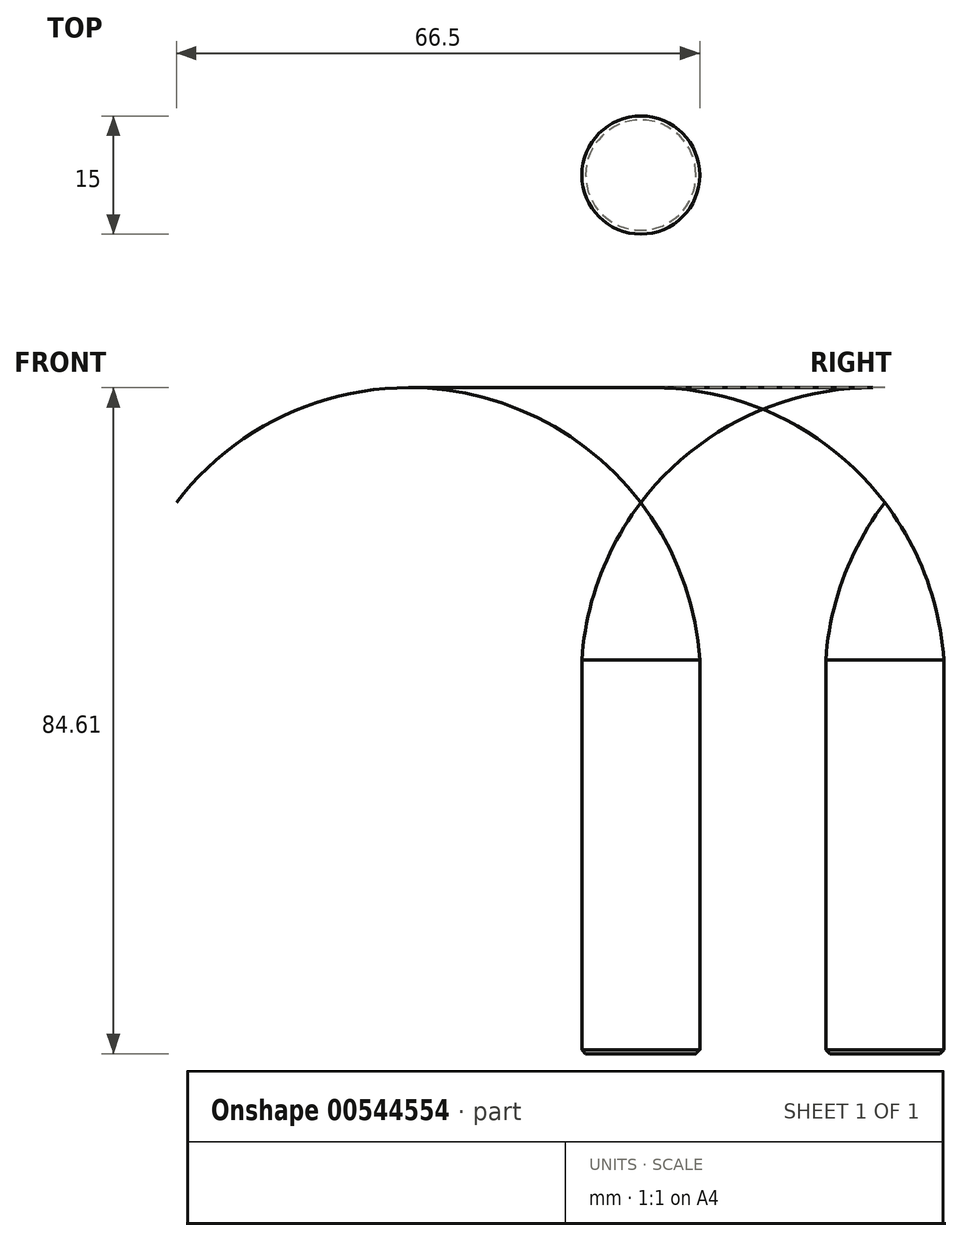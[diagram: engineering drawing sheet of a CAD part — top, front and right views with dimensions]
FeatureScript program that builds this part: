
annotation { "Feature Type Name" : "Feature", "Feature Type Description" : "" }
export const myFeature = defineFeature(function(context is Context, id is Id, definition is map)
    precondition{}
    {
        {
            var Q0;
            Q0=qCreatedBy(makeId("Front.planeOp"),FACE);
            var sketch = newSketch(context, id + "F0", { "sketchPlane" : qUnion([Q0])});
            skLineSegment(sketch, "E0", {"start": v(0, 0) * mm, "end": v(0, 20) * mm});
            skLineSegment(sketch, "E1", {"start": v(0, 0) * mm, "end": v(7.5, 0) * mm});
            skArc(sketch, "E2", {"start": v(7.5, 0) * mm, "mid": v(5.22, 10.55) * mm, "end": v(0, 20) * mm});
            skSolve(sketch);
        }
        {
            var Q0;
            Q0=makeQuery(id+"F0.imprint","IMPRINT",FACE,{"disambiguationData":[TD([[makeQuery(id+"F0.imprint","IMPRINT",EDGE,{"derivedFrom":sQuery(id+"F0.wireOp",EDGE,"E0")}),-1.0]])]});
            var Q1;
            Q1=sQuery(id+"F0.wireOp",EDGE,"E0");
            revolve(context, id + "F1", {"entities" : qUnion([Q0]), "axis" : qUnion([Q1]), "revolveType" : RevolveType.FULL});
        }
        {
            var Q0;
            Q0=qCreatedBy(makeId("Top.planeOp"),FACE);
            var sketch = newSketch(context, id + "F2", { "sketchPlane" : qUnion([Q0])});
            skCircle(sketch, "E3", {"center": v(0, 0) * mm, "radius": 7.5 * mm});
            skSolve(sketch);
        }
        {
            var Q0;
            Q0=makeQuery(id+"F2.imprint","IMPRINT",FACE,{"disambiguationData":[TD([[makeQuery(id+"F2.imprint","IMPRINT",EDGE,{"derivedFrom":sQuery(id+"F2.wireOp",EDGE,"E3")}),1.0]])]});
            extrude(context, id + "F3", {"entities" : qUnion([Q0]), "operationType" : NewBodyOperationType.ADD, "oppositeDirection" : true, "depth" : 50 * mm, "offsetDistance" : 25 * mm});
        }
        {
            var Q0;
            Q0=makeQuery(id+"F3.opExtrude","CAP_FACE",FACE,{"disambiguationData":[OSD([sQuery(id+"F2.wireOp",EDGE,"E3")])],"isStart":false});
            chamfer(context, id + "F4", {"entities" : qUnion([Q0]), "width" : 0.5 * mm, "tangentPropagation" : true});
        }
    });
